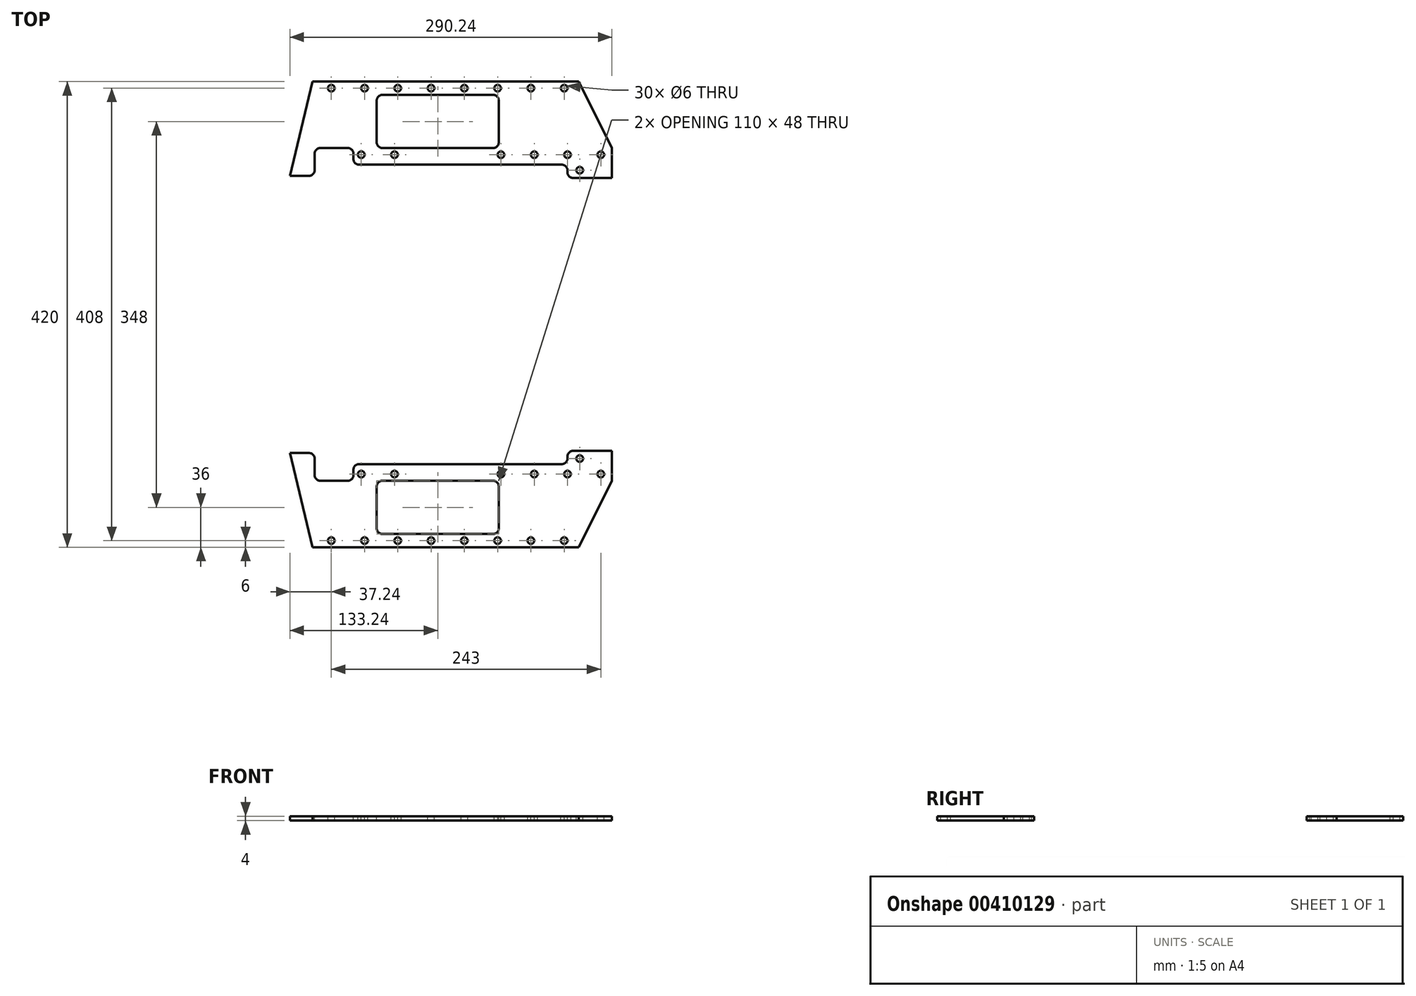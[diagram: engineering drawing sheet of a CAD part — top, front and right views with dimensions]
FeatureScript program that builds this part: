
annotation { "Feature Type Name" : "Feature", "Feature Type Description" : "" }
export const myFeature = defineFeature(function(context is Context, id is Id, definition is map)
    precondition{}
    {
        {
            var Q0;
            Q0=qCreatedBy(makeId("Top.planeOp"),FACE);
            var sketch = newSketch(context, id + "F0", { "sketchPlane" : qUnion([Q0])});
            skLineSegment(sketch, "E0.bottom", {"start": v(0, 0) * mm, "end": v(320, 0) * mm});
            skLineSegment(sketch, "E0.top", {"start": v(0, 420) * mm, "end": v(320, 420) * mm});
            skLineSegment(sketch, "E0.left", {"start": v(0, 0) * mm, "end": v(0, 420) * mm});
            skLineSegment(sketch, "E0.right", {"start": v(320, 0) * mm, "end": v(320, 420) * mm});
            skSolve(sketch);
        }
        {
            var Q0;
            Q0=qSketchRegion(id+"F0",true);
            extrude(context, id + "F1", {"entities" : qUnion([Q0]), "depth" : 4 * mm});
        }
        {
            var Q0;
            Q0=makeQuery(id+"F1.opExtrude","CAP_FACE",FACE,{"disambiguationData":[OSD([sQuery(id+"F0.wireOp",EDGE,"E0.bottom"),sQuery(id+"F0.wireOp",EDGE,"E0.top"),sQuery(id+"F0.wireOp",EDGE,"E0.left"),sQuery(id+"F0.wireOp",EDGE,"E0.right")])],"isStart":false});
            var sketch = newSketch(context, id + "F2", { "sketchPlane" : qUnion([Q0])});
            skLineSegment(sketch, "E1", {"start": v(290, 420) * mm, "end": v(320, 360) * mm});
            skLineSegment(sketch, "E2", {"start": v(290, 420) * mm, "end": v(320, 420) * mm});
            skLineSegment(sketch, "E3", {"start": v(320, 420) * mm, "end": v(320, 360) * mm});
            skLineSegment(sketch, "E4", {"start": v(290, 0) * mm, "end": v(320, 60) * mm});
            skLineSegment(sketch, "E5", {"start": v(290, 0) * mm, "end": v(320, 0) * mm});
            skLineSegment(sketch, "E6", {"start": v(320, 0) * mm, "end": v(320, 60) * mm});
            skLineSegment(sketch, "E7", {"start": v(0, 210) * mm, "end": v(320, 210) * mm, "construction": true});
            skLineSegment(sketch, "E8", {"start": v(163, 384) * mm, "end": v(163, 36) * mm, "construction": true});
            skPoint(sketch, "E9", {"position": v(163, 210) * mm});
            skLineSegment(sketch, "E10.bottom", {"start": v(213, 360) * mm, "end": v(113, 360) * mm});
            skLineSegment(sketch, "E10.top", {"start": v(213, 408) * mm, "end": v(113, 408) * mm});
            skLineSegment(sketch, "E10.left", {"start": v(218, 365) * mm, "end": v(218, 403) * mm});
            skLineSegment(sketch, "E10.right", {"start": v(108, 365) * mm, "end": v(108, 403) * mm});
            skPoint(sketch, "E10.middle", {"position": v(163, 384) * mm});
            skLineSegment(sketch, "E11.bottom", {"start": v(213, 12) * mm, "end": v(113, 12) * mm});
            skLineSegment(sketch, "E11.top", {"start": v(213, 60) * mm, "end": v(113, 60) * mm});
            skLineSegment(sketch, "E11.left", {"start": v(218, 17) * mm, "end": v(218, 55) * mm});
            skLineSegment(sketch, "E11.right", {"start": v(108, 17) * mm, "end": v(108, 55) * mm});
            skPoint(sketch, "E11.middle", {"position": v(163, 36) * mm});
            skPoint(sketch, "E12.visualSharp", {"position": v(108, 408) * mm});
            skArc(sketch, "E12.filletArc", {"start": v(113, 408) * mm, "mid": v(109.46, 406.54) * mm, "end": v(108, 403) * mm});
            skPoint(sketch, "E13.visualSharp", {"position": v(218, 408) * mm});
            skArc(sketch, "E13.filletArc", {"start": v(218, 403) * mm, "mid": v(216.54, 406.54) * mm, "end": v(213, 408) * mm});
            skPoint(sketch, "E14.visualSharp", {"position": v(108, 360) * mm});
            skArc(sketch, "E14.filletArc", {"start": v(108, 365) * mm, "mid": v(109.46, 361.46) * mm, "end": v(113, 360) * mm});
            skPoint(sketch, "E15.visualSharp", {"position": v(218, 360) * mm});
            skArc(sketch, "E15.filletArc", {"start": v(213, 360) * mm, "mid": v(216.54, 361.46) * mm, "end": v(218, 365) * mm});
            skPoint(sketch, "E16.visualSharp", {"position": v(218, 60) * mm});
            skArc(sketch, "E16.filletArc", {"start": v(218, 55) * mm, "mid": v(216.54, 58.54) * mm, "end": v(213, 60) * mm});
            skPoint(sketch, "E17.visualSharp", {"position": v(218, 12) * mm});
            skArc(sketch, "E17.filletArc", {"start": v(213, 12) * mm, "mid": v(216.54, 13.46) * mm, "end": v(218, 17) * mm});
            skPoint(sketch, "E18.visualSharp", {"position": v(108, 12) * mm});
            skArc(sketch, "E18.filletArc", {"start": v(108, 17) * mm, "mid": v(109.46, 13.46) * mm, "end": v(113, 12) * mm});
            skPoint(sketch, "E19.visualSharp", {"position": v(108, 60) * mm});
            skArc(sketch, "E19.filletArc", {"start": v(113, 60) * mm, "mid": v(109.46, 58.54) * mm, "end": v(108, 55) * mm});
            skLineSegment(sketch, "E20", {"start": v(0, 210) * mm, "end": v(50, 420) * mm});
            skLineSegment(sketch, "E21", {"start": v(0, 210) * mm, "end": v(50, 0) * mm});
            skLineSegment(sketch, "E22", {"start": v(50, 420) * mm, "end": v(0, 420) * mm});
            skLineSegment(sketch, "E23", {"start": v(0, 420) * mm, "end": v(0, 0) * mm});
            skLineSegment(sketch, "E24", {"start": v(0, 0) * mm, "end": v(50, 0) * mm});
            skSolve(sketch);
        }
        {
            var Q0;
            Q0=qSketchRegion(id+"F2",true);
            var Q1;
            Q1=makeQuery(id+"F1.opExtrude","CAP_FACE",FACE,{"disambiguationData":[OSD([sQuery(id+"F0.wireOp",EDGE,"E0.bottom"),sQuery(id+"F0.wireOp",EDGE,"E0.top"),sQuery(id+"F0.wireOp",EDGE,"E0.left"),sQuery(id+"F0.wireOp",EDGE,"E0.right")])],"isStart":true});
            extrude(context, id + "F3", {"entities" : qUnion([Q0]), "operationType" : NewBodyOperationType.REMOVE, "endBound" : BoundingType.UP_TO_SURFACE, "oppositeDirection" : true, "endBoundEntityFace" : qUnion([Q1]), "depth" : 25 * mm});
        }
        {
            var Q0;
            Q0=makeQuery(id+"F1.opExtrude","CAP_FACE",FACE,{"disambiguationData":[OSD([sQuery(id+"F0.wireOp",EDGE,"E0.bottom"),sQuery(id+"F0.wireOp",EDGE,"E0.top"),sQuery(id+"F0.wireOp",EDGE,"E0.left"),sQuery(id+"F0.wireOp",EDGE,"E0.right")])],"isStart":false});
            var sketch = newSketch(context, id + "F4", { "sketchPlane" : qUnion([Q0])});
            skLineSegment(sketch, "E25", {"start": v(67, 6) * mm, "end": v(277, 6) * mm, "construction": true});
            skCircle(sketch, "E26", {"center": v(67, 6) * mm, "radius": 3 * mm});
            skCircle(sketch, "E27.1.0.0", {"center": v(97, 6) * mm, "radius": 3 * mm});
            skCircle(sketch, "E27.2.0.0", {"center": v(127, 6) * mm, "radius": 3 * mm});
            skCircle(sketch, "E27.3.0.0", {"center": v(157, 6) * mm, "radius": 3 * mm});
            skCircle(sketch, "E27.4.0.0", {"center": v(187, 6) * mm, "radius": 3 * mm});
            skCircle(sketch, "E27.5.0.0", {"center": v(217, 6) * mm, "radius": 3 * mm});
            skCircle(sketch, "E27.6.0.0", {"center": v(247, 6) * mm, "radius": 3 * mm});
            skCircle(sketch, "E27.7.0.0", {"center": v(277, 6) * mm, "radius": 3 * mm});
            skLineSegment(sketch, "E27.direction1", {"start": v(67, 6) * mm, "end": v(97, 6) * mm, "construction": true});
            skLineSegment(sketch, "E28", {"start": v(70, 66) * mm, "end": v(310, 66) * mm, "construction": true});
            skCircle(sketch, "E29", {"center": v(64, 66) * mm, "radius": 3 * mm});
            skCircle(sketch, "E30.1.0.0", {"center": v(94, 66) * mm, "radius": 3 * mm});
            skCircle(sketch, "E30.2.0.0", {"center": v(124, 66) * mm, "radius": 3 * mm});
            skCircle(sketch, "E30.3.0.0", {"center": v(160, 66) * mm, "radius": 3 * mm, "construction": true});
            skCircle(sketch, "E30.4.0.0", {"center": v(190, 66) * mm, "radius": 3 * mm, "construction": true});
            skCircle(sketch, "E30.5.0.0", {"center": v(220, 66) * mm, "radius": 3 * mm});
            skCircle(sketch, "E30.6.0.0", {"center": v(250, 66) * mm, "radius": 3 * mm});
            skCircle(sketch, "E30.7.0.0", {"center": v(280, 66) * mm, "radius": 3 * mm});
            skCircle(sketch, "E30.8.0.0", {"center": v(310, 66) * mm, "radius": 3 * mm});
            skLineSegment(sketch, "E30.direction1", {"start": v(64, 66) * mm, "end": v(94, 66) * mm, "construction": true});
            skLineSegment(sketch, "E31", {"start": v(0, 210) * mm, "end": v(320, 210) * mm, "construction": true});
            skCircle(sketch, "E32.MirrorC", {"center": v(67, 414) * mm, "radius": 3 * mm});
            skCircle(sketch, "E33.MirrorC", {"center": v(64, 354) * mm, "radius": 3 * mm});
            skCircle(sketch, "E34.MirrorC", {"center": v(97, 414) * mm, "radius": 3 * mm});
            skCircle(sketch, "E35.MirrorC", {"center": v(310, 354) * mm, "radius": 3 * mm});
            skCircle(sketch, "E36.MirrorC", {"center": v(277, 414) * mm, "radius": 3 * mm});
            skCircle(sketch, "E37.MirrorC", {"center": v(94, 354) * mm, "radius": 3 * mm});
            skCircle(sketch, "E38.MirrorC", {"center": v(220, 354) * mm, "radius": 3 * mm});
            skLineSegment(sketch, "E39.MirrorCS", {"start": v(64, 354) * mm, "end": v(94, 354) * mm, "construction": true});
            skCircle(sketch, "E40.MirrorC", {"center": v(280, 354) * mm, "radius": 3 * mm});
            skCircle(sketch, "E41.MirrorC", {"center": v(124, 354) * mm, "radius": 3 * mm});
            skCircle(sketch, "E42.MirrorC", {"center": v(160, 354) * mm, "radius": 3 * mm, "construction": true});
            skCircle(sketch, "E43.MirrorC", {"center": v(190, 354) * mm, "radius": 3 * mm, "construction": true});
            skCircle(sketch, "E44.MirrorC", {"center": v(127, 414) * mm, "radius": 3 * mm});
            skCircle(sketch, "E45.MirrorC", {"center": v(250, 354) * mm, "radius": 3 * mm});
            skCircle(sketch, "E46.MirrorC", {"center": v(157, 414) * mm, "radius": 3 * mm});
            skCircle(sketch, "E47.MirrorC", {"center": v(187, 414) * mm, "radius": 3 * mm});
            skCircle(sketch, "E48.MirrorC", {"center": v(217, 414) * mm, "radius": 3 * mm});
            skCircle(sketch, "E49.MirrorC", {"center": v(247, 414) * mm, "radius": 3 * mm});
            skLineSegment(sketch, "E50.MirrorCS", {"start": v(67, 414) * mm, "end": v(277, 414) * mm, "construction": true});
            skLineSegment(sketch, "E51.MirrorCS", {"start": v(67, 414) * mm, "end": v(97, 414) * mm, "construction": true});
            skLineSegment(sketch, "E52.MirrorCS", {"start": v(70, 354) * mm, "end": v(310, 354) * mm, "construction": true});
            skSolve(sketch);
        }
        {
            var Q0;
            Q0=qSketchRegion(id+"F4",true);
            extrude(context, id + "F5", {"entities" : qUnion([Q0]), "operationType" : NewBodyOperationType.REMOVE, "oppositeDirection" : true, "depth" : 25 * mm});
        }
        {
            var Q0;
            Q0=makeQuery(id+"F1.opExtrude","CAP_FACE",FACE,{"disambiguationData":[OSD([sQuery(id+"F0.wireOp",EDGE,"E0.bottom"),sQuery(id+"F0.wireOp",EDGE,"E0.top"),sQuery(id+"F0.wireOp",EDGE,"E0.left"),sQuery(id+"F0.wireOp",EDGE,"E0.right")])],"isStart":false});
            var sketch = newSketch(context, id + "F6", { "sketchPlane" : qUnion([Q0])});
            skLineSegment(sketch, "E53", {"start": v(0, 210) * mm, "end": v(320, 210) * mm, "construction": true});
            skLineSegment(sketch, "E54", {"start": v(108, 365) * mm, "end": v(108, 55) * mm, "construction": true});
            skLineSegment(sketch, "E55", {"start": v(121, 90) * mm, "end": v(121, 330.2) * mm, "construction": true});
            skCircle(sketch, "E56", {"center": v(121, 90) * mm, "radius": 3 * mm});
            skCircle(sketch, "E57.0.1.0", {"center": v(121, 130) * mm, "radius": 3 * mm});
            skCircle(sketch, "E57.0.2.0", {"center": v(121, 170) * mm, "radius": 3 * mm});
            skCircle(sketch, "E57.1.0.0", {"center": v(206, 90) * mm, "radius": 3 * mm});
            skCircle(sketch, "E57.1.1.0", {"center": v(206, 130) * mm, "radius": 3 * mm});
            skCircle(sketch, "E57.1.2.0", {"center": v(206, 170) * mm, "radius": 3 * mm});
            skCircle(sketch, "E57.2.0.0", {"center": v(291, 80) * mm, "radius": 3 * mm});
            skCircle(sketch, "E57.2.1.0", {"center": v(291, 120) * mm, "radius": 3 * mm});
            skCircle(sketch, "E57.2.2.0", {"center": v(291, 160) * mm, "radius": 3 * mm});
            skLineSegment(sketch, "E57.direction1", {"start": v(121, 90) * mm, "end": v(206, 90) * mm, "construction": true});
            skLineSegment(sketch, "E57.direction2", {"start": v(121, 90) * mm, "end": v(121, 130) * mm, "construction": true});
            skCircle(sketch, "E58.MirrorC", {"center": v(121, 330) * mm, "radius": 3 * mm});
            skCircle(sketch, "E59.MirrorC", {"center": v(121, 290) * mm, "radius": 3 * mm});
            skCircle(sketch, "E60.MirrorC", {"center": v(206, 330) * mm, "radius": 3 * mm});
            skCircle(sketch, "E61.MirrorC", {"center": v(206, 250) * mm, "radius": 3 * mm});
            skCircle(sketch, "E62.MirrorC", {"center": v(291, 340) * mm, "radius": 3 * mm});
            skCircle(sketch, "E63.MirrorC", {"center": v(121, 250) * mm, "radius": 3 * mm});
            skCircle(sketch, "E64.MirrorC", {"center": v(206, 290) * mm, "radius": 3 * mm});
            skCircle(sketch, "E65.MirrorC", {"center": v(291, 300) * mm, "radius": 3 * mm});
            skCircle(sketch, "E66.MirrorC", {"center": v(291, 260) * mm, "radius": 3 * mm});
            skLineSegment(sketch, "E67.MirrorCS", {"start": v(121, 330) * mm, "end": v(121, 290) * mm, "construction": true});
            skLineSegment(sketch, "E68.MirrorCS", {"start": v(121, 330) * mm, "end": v(206, 330) * mm, "construction": true});
            skSolve(sketch);
        }
        {
            var Q0;
            Q0=qSketchRegion(id+"F6",true);
            extrude(context, id + "F7", {"entities" : qUnion([Q0]), "operationType" : NewBodyOperationType.REMOVE, "oppositeDirection" : true, "depth" : 25 * mm});
        }
        {
            var Q0;
            Q0=makeQuery(id+"F1.opExtrude","CAP_FACE",FACE,{"disambiguationData":[OSD([sQuery(id+"F0.wireOp",EDGE,"E0.bottom"),sQuery(id+"F0.wireOp",EDGE,"E0.top"),sQuery(id+"F0.wireOp",EDGE,"E0.left"),sQuery(id+"F0.wireOp",EDGE,"E0.right")])],"isStart":false});
            var sketch = newSketch(context, id + "F8", { "sketchPlane" : qUnion([Q0])});
            skLineSegment(sketch, "E69", {"start": v(0, 210) * mm, "end": v(320, 210) * mm, "construction": true});
            skCircle(sketch, "E70", {"center": v(15, 210) * mm, "radius": 3 * mm});
            skCircle(sketch, "E71.1.0.0", {"center": v(45, 210) * mm, "radius": 3 * mm});
            skLineSegment(sketch, "E71.direction1", {"start": v(15, 210) * mm, "end": v(45, 210) * mm, "construction": true});
            skSolve(sketch);
        }
        {
            var Q0;
            Q0=qSketchRegion(id+"F8",true);
            extrude(context, id + "F9", {"entities" : qUnion([Q0]), "operationType" : NewBodyOperationType.REMOVE, "oppositeDirection" : true, "depth" : 25 * mm});
        }
        {
            var Q0;
            Q0=makeQuery(id+"F1.opExtrude","CAP_FACE",FACE,{"disambiguationData":[OSD([sQuery(id+"F0.wireOp",EDGE,"E0.bottom"),sQuery(id+"F0.wireOp",EDGE,"E0.top"),sQuery(id+"F0.wireOp",EDGE,"E0.left"),sQuery(id+"F0.wireOp",EDGE,"E0.right")])],"isStart":false});
            var sketch = newSketch(context, id + "F10", { "sketchPlane" : qUnion([Q0])});
            skLineSegment(sketch, "E72", {"start": v(0, 210) * mm, "end": v(320, 210) * mm, "construction": true});
            skLineSegment(sketch, "E73.right", {"start": v(87, 355) * mm, "end": v(87, 350) * mm});
            skLineSegment(sketch, "E74", {"start": v(0, 335) * mm, "end": v(47, 335) * mm});
            skLineSegment(sketch, "E75", {"start": v(52, 340) * mm, "end": v(52, 355) * mm});
            skLineSegment(sketch, "E76", {"start": v(57, 360) * mm, "end": v(82, 360) * mm});
            skLineSegment(sketch, "E77", {"start": v(280, 340) * mm, "end": v(280, 338) * mm});
            skLineSegment(sketch, "E78", {"start": v(285, 333) * mm, "end": v(320, 333) * mm});
            skLineSegment(sketch, "E79", {"start": v(320, 333) * mm, "end": v(320, 210) * mm});
            skPoint(sketch, "E80.visualSharp", {"position": v(52, 335) * mm});
            skArc(sketch, "E80.filletArc", {"start": v(47, 335) * mm, "mid": v(50.54, 336.46) * mm, "end": v(52, 340) * mm});
            skPoint(sketch, "E81.newPointA", {"position": v(52, 360) * mm});
            skPoint(sketch, "E81.newPointB", {"position": v(0, 360) * mm});
            skArc(sketch, "E81.filletArc", {"start": v(57, 360) * mm, "mid": v(53.46, 358.54) * mm, "end": v(52, 355) * mm});
            skPoint(sketch, "E82.visualSharp", {"position": v(87, 360) * mm});
            skArc(sketch, "E82.filletArc", {"start": v(87, 355) * mm, "mid": v(85.54, 358.54) * mm, "end": v(82, 360) * mm});
            skArc(sketch, "E83.filletArc", {"start": v(87, 350) * mm, "mid": v(88.46, 346.46) * mm, "end": v(92, 345) * mm});
            skPoint(sketch, "E84.newPointA", {"position": v(280, 345) * mm});
            skPoint(sketch, "E84.newPointB", {"position": v(320, 345) * mm});
            skArc(sketch, "E84.filletArc", {"start": v(280, 340) * mm, "mid": v(278.54, 343.54) * mm, "end": v(275, 345) * mm});
            skPoint(sketch, "E85.visualSharp", {"position": v(280, 333) * mm});
            skArc(sketch, "E85.filletArc", {"start": v(280, 338) * mm, "mid": v(281.46, 334.46) * mm, "end": v(285, 333) * mm});
            skLineSegment(sketch, "E86", {"start": v(0, 335) * mm, "end": v(0, 210) * mm});
            skLineSegment(sketch, "E87", {"start": v(92, 345) * mm, "end": v(275, 345) * mm});
            skArc(sketch, "E88.MirrorCS", {"start": v(47, 85) * mm, "mid": v(50.54, 83.54) * mm, "end": v(52, 80) * mm});
            skArc(sketch, "E89.MirrorCS", {"start": v(87, 70) * mm, "mid": v(88.46, 73.54) * mm, "end": v(92, 75) * mm});
            skArc(sketch, "E90.MirrorCS", {"start": v(57, 60) * mm, "mid": v(53.46, 61.46) * mm, "end": v(52, 65) * mm});
            skLineSegment(sketch, "E91.MirrorCS", {"start": v(87, 65) * mm, "end": v(87, 70) * mm});
            skArc(sketch, "E92.MirrorCS", {"start": v(87, 65) * mm, "mid": v(85.54, 61.46) * mm, "end": v(82, 60) * mm});
            skLineSegment(sketch, "E93.MirrorCS", {"start": v(280, 80) * mm, "end": v(280, 82) * mm});
            skArc(sketch, "E94.MirrorCS", {"start": v(280, 82) * mm, "mid": v(281.46, 85.54) * mm, "end": v(285, 87) * mm});
            skArc(sketch, "E95.MirrorCS", {"start": v(280, 80) * mm, "mid": v(278.54, 76.46) * mm, "end": v(275, 75) * mm});
            skLineSegment(sketch, "E96.MirrorCS", {"start": v(52, 80) * mm, "end": v(52, 65) * mm});
            skLineSegment(sketch, "E97.MirrorCS", {"start": v(57, 60) * mm, "end": v(82, 60) * mm});
            skPoint(sketch, "E98.MirrorP", {"position": v(320, 75) * mm});
            skLineSegment(sketch, "E99.MirrorCS", {"start": v(320, 87) * mm, "end": v(320, 210) * mm});
            skPoint(sketch, "E100.MirrorP", {"position": v(52, 60) * mm});
            skPoint(sketch, "E101.MirrorP", {"position": v(52, 85) * mm});
            skPoint(sketch, "E102.MirrorP", {"position": v(87, 60) * mm});
            skPoint(sketch, "E103.MirrorP", {"position": v(280, 87) * mm});
            skLineSegment(sketch, "E104.MirrorCS", {"start": v(92, 75) * mm, "end": v(275, 75) * mm});
            skPoint(sketch, "E105.MirrorP", {"position": v(0, 60) * mm});
            skLineSegment(sketch, "E106.MirrorCS", {"start": v(0, 85) * mm, "end": v(0, 210) * mm});
            skLineSegment(sketch, "E107.MirrorCS", {"start": v(285, 87) * mm, "end": v(320, 87) * mm});
            skPoint(sketch, "E108.MirrorP", {"position": v(280, 75) * mm});
            skLineSegment(sketch, "E109.MirrorCS", {"start": v(0, 85) * mm, "end": v(47, 85) * mm});
            skSolve(sketch);
        }
        {
            var Q0;
            Q0 = qSketchRegion(id + "F10", true);
            extrude(context, id + "F11", {"entities" : qUnion([Q0]), "operationType" : NewBodyOperationType.REMOVE, "oppositeDirection" : true, "depth" : 25 * mm});
        }
    });
